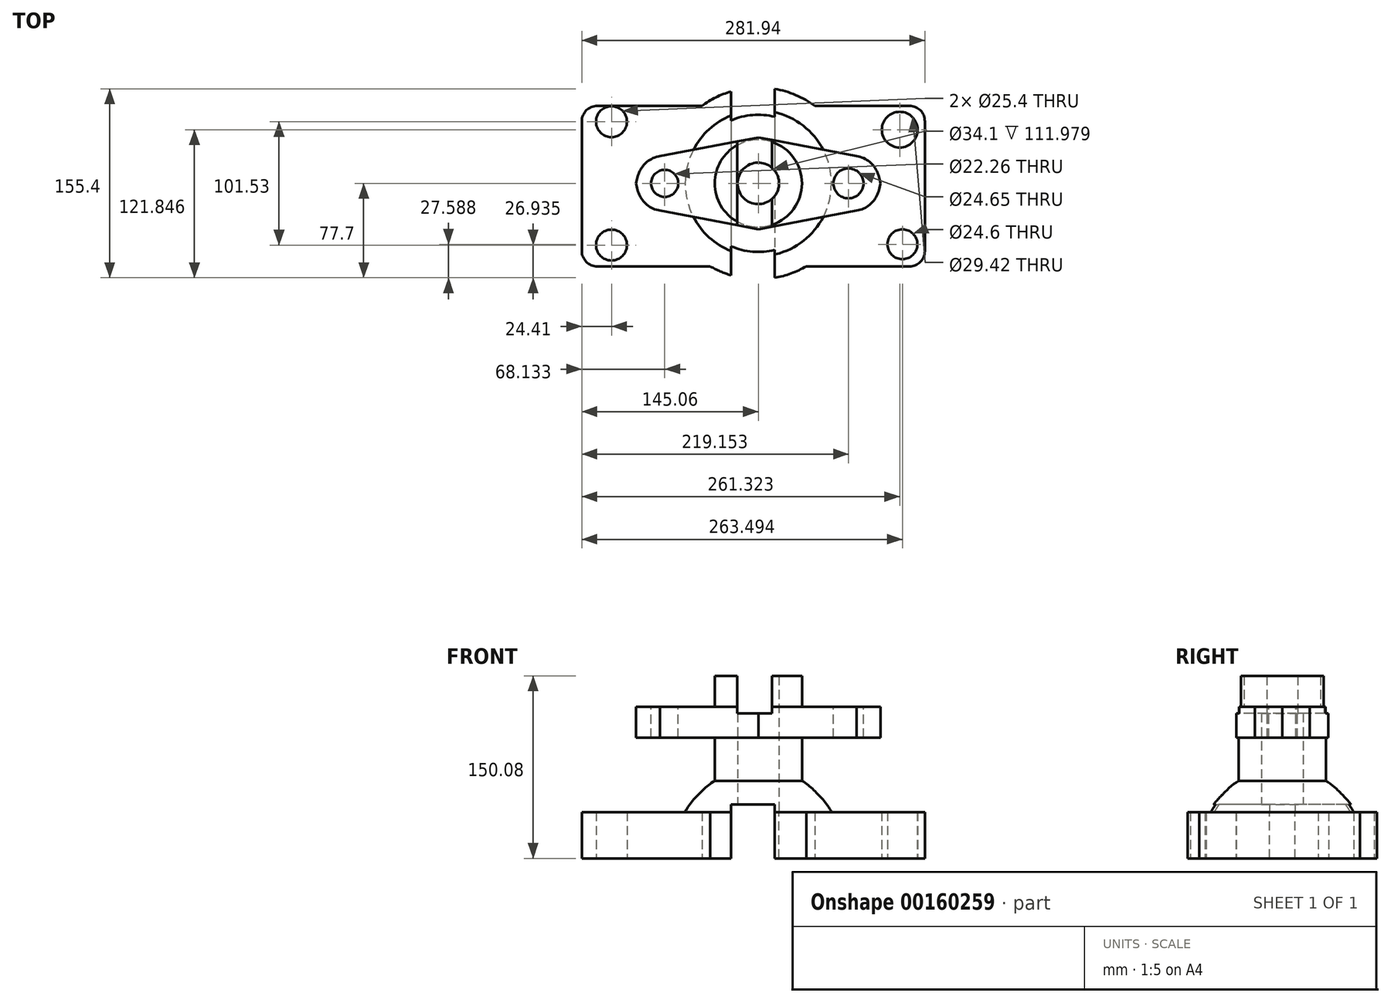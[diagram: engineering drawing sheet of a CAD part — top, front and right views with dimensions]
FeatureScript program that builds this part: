
annotation { "Feature Type Name" : "Feature", "Feature Type Description" : "" }
export const myFeature = defineFeature(function(context is Context, id is Id, definition is map)
    precondition{}
    {
        {
            var Q0;
            Q0=qCreatedBy(makeId("Top.planeOp"),FACE);
            var sketch = newSketch(context, id + "F0", { "sketchPlane" : qUnion([Q0])});
            skLineSegment(sketch, "E0.bottom", {"start": v(-132.36, 63.8) * mm, "end": v(-132.36, 63.8) * mm});
            skLineSegment(sketch, "E0.top", {"start": v(-132.36, -68.28) * mm, "end": v(-131.1, -68.28) * mm});
            skLineSegment(sketch, "E0.left", {"start": v(-145.06, 51.1) * mm, "end": v(-145.06, -55.58) * mm});
            skLineSegment(sketch, "E0.right", {"start": v(136.88, 51.1) * mm, "end": v(136.88, -55.58) * mm});
            skPoint(sketch, "E1.visualSharp", {"position": v(-145.06, 63.8) * mm});
            skArc(sketch, "E1.filletArc", {"start": v(-132.36, 63.8) * mm, "mid": v(-141.34, 60.08) * mm, "end": v(-145.06, 51.1) * mm});
            skPoint(sketch, "E2.visualSharp", {"position": v(-145.06, -68.28) * mm});
            skArc(sketch, "E2.filletArc", {"start": v(-145.06, -55.58) * mm, "mid": v(-141.34, -64.56) * mm, "end": v(-132.36, -68.28) * mm});
            skPoint(sketch, "E3.visualSharp", {"position": v(136.88, -68.28) * mm});
            skArc(sketch, "E3.filletArc", {"start": v(124.18, -68.28) * mm, "mid": v(133.16, -64.56) * mm, "end": v(136.88, -55.58) * mm});
            skPoint(sketch, "E4.visualSharp", {"position": v(136.88, 63.8) * mm});
            skArc(sketch, "E4.filletArc", {"start": v(136.88, 51.1) * mm, "mid": v(133.16, 60.08) * mm, "end": v(124.18, 63.8) * mm});
            skLineSegment(sketch, "E5", {"start": v(-129.85, -68.28) * mm, "end": v(124.15, -68.28) * mm});
            skLineSegment(sketch, "E6", {"start": v(124.15, -68.28) * mm, "end": v(124.18, -68.28) * mm});
            skLineSegment(sketch, "E7", {"start": v(-132.36, 63.8) * mm, "end": v(124.18, 63.8) * mm});
            skLineSegment(sketch, "E8", {"start": v(-131.1, -68.28) * mm, "end": v(-129.85, -68.28) * mm});
            skCircle(sketch, "E9", {"center": v(-120.65, -50.77) * mm, "radius": 12.7 * mm});
            skArc(sketch, "E10", {"start": v(-119.4, 38.13) * mm, "mid": v(-119.8, 38.1) * mm, "end": v(-120.2, 38.07) * mm});
            skArc(sketch, "E11", {"start": v(-120.2, 38.07) * mm, "mid": v(-121.5, 63.44) * mm, "end": v(-119.4, 38.13) * mm});
            skCircle(sketch, "E12", {"center": v(118.43, -50.11) * mm, "radius": 12.3 * mm});
            skCircle(sketch, "E13", {"center": v(116.26, 44.15) * mm, "radius": 14.7 * mm});
            skSolve(sketch);
        }
        {
            var Q0;
            Q0=makeQuery(id+"F0.imprint","IMPRINT",FACE,{"disambiguationData":[TD([[makeQuery(id+"F0.imprint","IMPRINT",EDGE,{"derivedFrom":sQuery(id+"F0.wireOp",EDGE,"E0.top")}),1.0]])]});
            var sketch = newSketch(context, id + "F1", { "sketchPlane" : qUnion([Q0])});
            skCircle(sketch, "E14", {"center": v(117.05, 46.4) * mm, "radius": 12.7 * mm});
            skCircle(sketch, "E15", {"center": v(0, 0) * mm, "radius": 78.87 * mm});
            skSolve(sketch);
        }
        {
            var Q0;
            Q0=makeQuery(id+"F0.imprint","IMPRINT",FACE,{"disambiguationData":[TD([[makeQuery(id+"F0.imprint","IMPRINT",EDGE,{"derivedFrom":sQuery(id+"F0.wireOp",EDGE,"E0.top")}),1.0]])]});
            extrude(context, id + "F2", {"entities" : qUnion([Q0]), "depth" : 38.1 * mm});
        }
        {
            var Q0;
            {var subQ0=sQuery(id+"F1.wireOp",EDGE,"E15");var subQ1=makeQuery(id+"F0.imprint","IMPRINT",EDGE,{"derivedFrom":sQuery(id+"F0.wireOp",EDGE,"E7")});var subQ2=makeQuery(id+"F1.imprint","INTERSECT",VERTEX,{"disambiguationData":[OD(0.0)],"derivedFrom":[subQ1,subQ0]});Q0=makeQuery(id+"F1.imprint","IMPRINT",FACE,{"disambiguationData":[TD([[makeQuery(id+"F1.imprint","IMPRINT",EDGE,{"disambiguationData":[TD([[subQ2,1.0]])],"derivedFrom":subQ0}),1.0]])]});}
            var Q1;
            {var subQ0=sQuery(id+"F1.wireOp",EDGE,"E15");var subQ1=makeQuery(id+"F0.imprint","IMPRINT",EDGE,{"derivedFrom":sQuery(id+"F0.wireOp",EDGE,"E5")});var subQ2=makeQuery(id+"F1.imprint","INTERSECT",VERTEX,{"disambiguationData":[OD(0.0)],"derivedFrom":[subQ1,subQ0]});Q1=makeQuery(id+"F1.imprint","IMPRINT",FACE,{"disambiguationData":[TD([[makeQuery(id+"F1.imprint","IMPRINT",EDGE,{"disambiguationData":[TD([[subQ2,-1.0]])],"derivedFrom":subQ0}),1.0]])]});}
            extrude(context, id + "F3", {"entities" : qUnion([Q0, Q1]), "operationType" : NewBodyOperationType.ADD, "depth" : 38.1 * mm});
        }
        {
            var Q0;
            Q0=qCreatedBy(makeId("Front.planeOp"),FACE);
            var sketch = newSketch(context, id + "F4", { "sketchPlane" : qUnion([Q0])});
            skLineSegment(sketch, "E16", {"start": v(60.1, 38.1) * mm, "end": v(0, 38.1) * mm});
            skLineSegment(sketch, "E17", {"start": v(0, 38.1) * mm, "end": v(0, 61.4) * mm});
            skLineSegment(sketch, "E18", {"start": v(0, 61.4) * mm, "end": v(0, 63.72) * mm});
            skLineSegment(sketch, "E19", {"start": v(0, 63.72) * mm, "end": v(35.82, 63.72) * mm});
            skFitSpline(sketch, "E20", {"points": [v(35.82, 63.72) * mm, v(49.5, 52.16) * mm, v(60.1, 38.1) * mm], "startDerivative": vector(35.68, -20.72) * mm, "endDerivative": vector(19.73, -40.62) * mm});
            skSolve(sketch);
        }
        {
            var Q0;
            Q0 = qSketchRegion(id + "F4", true);
            var Q1;
            Q1=sQuery(id+"F4.wireOp",EDGE,"E17");
            revolve(context, id + "F5", {"entities" : qUnion([Q0]), "axis" : qUnion([Q1]), "revolveType" : RevolveType.FULL});
        }
        {
            var Q0;
            Q0=makeQuery(id+"F5.opRevolve","SWEPT_FACE",FACE,{"disambiguationData":[OSD([sQuery(id+"F4.wireOp",EDGE,"E19")])]});
            var sketch = newSketch(context, id + "F6", { "sketchPlane" : qUnion([Q0])});
            skCircle(sketch, "E21", {"center": v(0, 0) * mm, "radius": 35.88 * mm});
            skSolve(sketch);
        }
        {
            var Q0;
            Q0 = qSketchRegion(id + "F6", true);
            extrude(context, id + "F7", {"entities" : qUnion([Q0]), "operationType" : NewBodyOperationType.ADD, "depth" : 86.36 * mm});
        }
        {
            var Q0;
            Q0=makeQuery(id+"F7.opExtrude","CAP_FACE",FACE,{"disambiguationData":[OSD([sQuery(id+"F6.wireOp",EDGE,"E21")])],"isStart":false});
            cPlane(context, id + "F8", {"entities" : qUnion([Q0]), "cplaneType" : CPlaneType.OFFSET, "offset" : 25.4 * mm, "oppositeDirection" : true, "width" : 152.4 * mm, "height" : 152.4 * mm});
        }
        {
            var Q0;
            Q0=qCreatedBy(id+"F8.planeOp",FACE);
            var sketch = newSketch(context, id + "F9", { "sketchPlane" : qUnion([Q0])});
            skLineSegment(sketch, "E22", {"start": v(0, 37.8) * mm, "end": v(-80.67, 22.44) * mm});
            skFitSpline(sketch, "E23", {"points": [v(-80.67, 22.44) * mm, v(-95.14, 13.78) * mm, v(-100.47, 0) * mm], "startDerivative": vector(-37.1, -5.33) * mm, "endDerivative": vector(-5.84, -32.33) * mm});
            skLineSegment(sketch, "E24", {"start": v(-100.47, 0) * mm, "end": v(-92.9, 0) * mm});
            skFitSpline(sketch, "E25.MirrorCS", {"points": [v(-80.67, -22.44) * mm, v(-95.14, -13.78) * mm, v(-100.47, 0) * mm], "startDerivative": vector(-37.1, 5.33) * mm, "endDerivative": vector(-5.84, 32.33) * mm});
            skLineSegment(sketch, "E26.MirrorCS", {"start": v(0, -37.8) * mm, "end": v(-80.67, -22.44) * mm});
            skLineSegment(sketch, "E27", {"start": v(0, 37.8) * mm, "end": v(0, 31) * mm});
            skLineSegment(sketch, "E28.MirrorCS", {"start": v(0, 37.8) * mm, "end": v(80.67, 22.44) * mm});
            skFitSpline(sketch, "E29.MirrorCS", {"points": [v(80.67, 22.44) * mm, v(95.14, 13.78) * mm, v(100.47, 0) * mm], "startDerivative": vector(37.1, -5.33) * mm, "endDerivative": vector(5.84, -32.33) * mm});
            skFitSpline(sketch, "E30.MirrorCS", {"points": [v(80.67, -22.44) * mm, v(95.14, -13.78) * mm, v(100.47, 0) * mm], "startDerivative": vector(37.1, 5.33) * mm, "endDerivative": vector(5.84, 32.33) * mm});
            skLineSegment(sketch, "E31.MirrorCS", {"start": v(0, -37.8) * mm, "end": v(80.67, -22.44) * mm});
            skSolve(sketch);
        }
        {
            var Q0;
            Q0 = qSketchRegion(id + "F9", true);
            extrude(context, id + "F10", {"entities" : qUnion([Q0]), "operationType" : NewBodyOperationType.ADD, "oppositeDirection" : true, "depth" : 25.4 * mm});
        }
        {
            var Q0;
            Q0=makeQuery(id+"F10.opExtrude","CAP_FACE",FACE,{"disambiguationData":[OSD([sQuery(id+"F9.wireOp",EDGE,"E22"),sQuery(id+"F9.wireOp",EDGE,"E23"),sQuery(id+"F9.wireOp",EDGE,"E25.MirrorCS"),sQuery(id+"F9.wireOp",EDGE,"E26.MirrorCS"),sQuery(id+"F9.wireOp",EDGE,"E28.MirrorCS"),sQuery(id+"F9.wireOp",EDGE,"E29.MirrorCS"),sQuery(id+"F9.wireOp",EDGE,"E30.MirrorCS"),sQuery(id+"F9.wireOp",EDGE,"E31.MirrorCS")])],"isStart":true});
            var sketch = newSketch(context, id + "F11", { "sketchPlane" : qUnion([Q0])});
            skCircle(sketch, "E32", {"center": v(-76.93, 0) * mm, "radius": 11.13 * mm});
            skSolve(sketch);
        }
        {
            var Q0;
            Q0 = qSketchRegion(id + "F11", true);
            extrude(context, id + "F12", {"entities" : qUnion([Q0]), "operationType" : NewBodyOperationType.REMOVE, "oppositeDirection" : true, "depth" : 25.4 * mm});
        }
        {
            var Q0;
            Q0=makeQuery(id+"F7.opExtrude","CAP_FACE",FACE,{"disambiguationData":[OSD([sQuery(id+"F6.wireOp",EDGE,"E21")])],"isStart":false});
            var sketch = newSketch(context, id + "F13", { "sketchPlane" : qUnion([Q0])});
            skCircle(sketch, "E33", {"center": v(74.1, 0) * mm, "radius": 12.32 * mm});
            skCircle(sketch, "E34", {"center": v(103.82, 37.52) * mm, "radius": 11.45 * mm});
            skSolve(sketch);
        }
        {
            var Q0;
            Q0 = qSketchRegion(id + "F13", true);
            extrude(context, id + "F14", {"entities" : qUnion([Q0]), "operationType" : NewBodyOperationType.REMOVE, "oppositeDirection" : true, "depth" : 25.4 * mm});
        }
        {
            var Q0;
            Q0=makeQuery(id+"F13.imprint","IMPRINT",FACE,{"disambiguationData":[TD([[makeQuery(id+"F13.imprint","IMPRINT",EDGE,{"derivedFrom":sQuery(id+"F13.wireOp",EDGE,"E33")}),1.0]])]});
            extrude(context, id + "F15", {"entities" : qUnion([Q0]), "operationType" : NewBodyOperationType.REMOVE, "oppositeDirection" : true, "depth" : 65.4 * mm});
        }
        {
            var Q0;
            Q0=qCreatedBy(id+"F8.planeOp",FACE);
            var sketch = newSketch(context, id + "F16", { "sketchPlane" : qUnion([Q0])});
            skCircle(sketch, "E35", {"center": v(0, 0) * mm, "radius": 17.05 * mm});
            skSolve(sketch);
        }
        {
            var Q0;
            Q0 = qSketchRegion(id + "F16", true);
            extrude(context, id + "F17", {"entities" : qUnion([Q0]), "operationType" : NewBodyOperationType.REMOVE, "depth" : 46.35 * mm});
        }
        {
            var Q0;
            Q0 = qSketchRegion(id + "F16", true);
            extrude(context, id + "F18", {"entities" : qUnion([Q0]), "operationType" : NewBodyOperationType.REMOVE, "endBound" : BoundingType.THROUGH_ALL, "oppositeDirection" : true, "depth" : 183.5 * mm});
        }
        {
            var Q0;
            Q0=qCreatedBy(id+"F8.planeOp",FACE);
            var sketch = newSketch(context, id + "F19", { "sketchPlane" : qUnion([Q0])});
            skCircle(sketch, "E36", {"center": v(0, 0) * mm, "radius": 16.8 * mm});
            skSolve(sketch);
        }
        {
            var Q0;
            Q0 = qSketchRegion(id + "F19", true);
            extrude(context, id + "F20", {"entities" : qUnion([Q0]), "operationType" : NewBodyOperationType.REMOVE, "oppositeDirection" : true, "depth" : 132.71 * mm});
        }
        {
            var Q0;
            Q0=qCreatedBy(makeId("Front.planeOp"),FACE);
            cPlane(context, id + "F21", {"entities" : qUnion([Q0]), "cplaneType" : CPlaneType.OFFSET, "offset" : 101.6 * mm, "width" : 152.4 * mm, "height" : 152.4 * mm});
        }
        {
            var Q0;
            Q0=qCreatedBy(id+"F21.planeOp",FACE);
            var sketch = newSketch(context, id + "F22", { "sketchPlane" : qUnion([Q0])});
            skLineSegment(sketch, "E37.bottom", {"start": v(-22.41, 44.36) * mm, "end": v(13.53, 44.36) * mm});
            skLineSegment(sketch, "E37.top", {"start": v(-22.41, 0) * mm, "end": v(13.53, 0) * mm});
            skLineSegment(sketch, "E37.left", {"start": v(-22.41, 44.36) * mm, "end": v(-22.41, 0) * mm});
            skLineSegment(sketch, "E37.right", {"start": v(13.53, 44.36) * mm, "end": v(13.53, 0) * mm});
            skSolve(sketch);
        }
        {
            var Q0;
            Q0 = qSketchRegion(id + "F22", true);
            extrude(context, id + "F23", {"entities" : qUnion([Q0]), "operationType" : NewBodyOperationType.REMOVE, "oppositeDirection" : true, "depth" : 202.56 * mm});
        }
        {
            var Q0;
            Q0=qCreatedBy(id+"F21.planeOp",FACE);
            var sketch = newSketch(context, id + "F24", { "sketchPlane" : qUnion([Q0])});
            skLineSegment(sketch, "E38.bottom", {"start": v(-17.2, 155.06) * mm, "end": v(11.37, 155.06) * mm});
            skLineSegment(sketch, "E38.top", {"start": v(-17.2, 119.35) * mm, "end": v(11.37, 119.35) * mm});
            skLineSegment(sketch, "E38.left", {"start": v(-17.2, 155.06) * mm, "end": v(-17.2, 119.35) * mm});
            skLineSegment(sketch, "E38.right", {"start": v(11.37, 155.06) * mm, "end": v(11.37, 119.35) * mm});
            skSolve(sketch);
        }
        {
            var Q0;
            Q0=makeQuery(id+"F24.imprint","IMPRINT",FACE,{"disambiguationData":[TD([[makeQuery(id+"F24.imprint","IMPRINT",EDGE,{"derivedFrom":sQuery(id+"F24.wireOp",EDGE,"E38.bottom")}),-1.0]])]});
            extrude(context, id + "F25", {"entities" : qUnion([Q0]), "operationType" : NewBodyOperationType.REMOVE, "oppositeDirection" : true, "depth" : 154.3 * mm});
        }
    });
